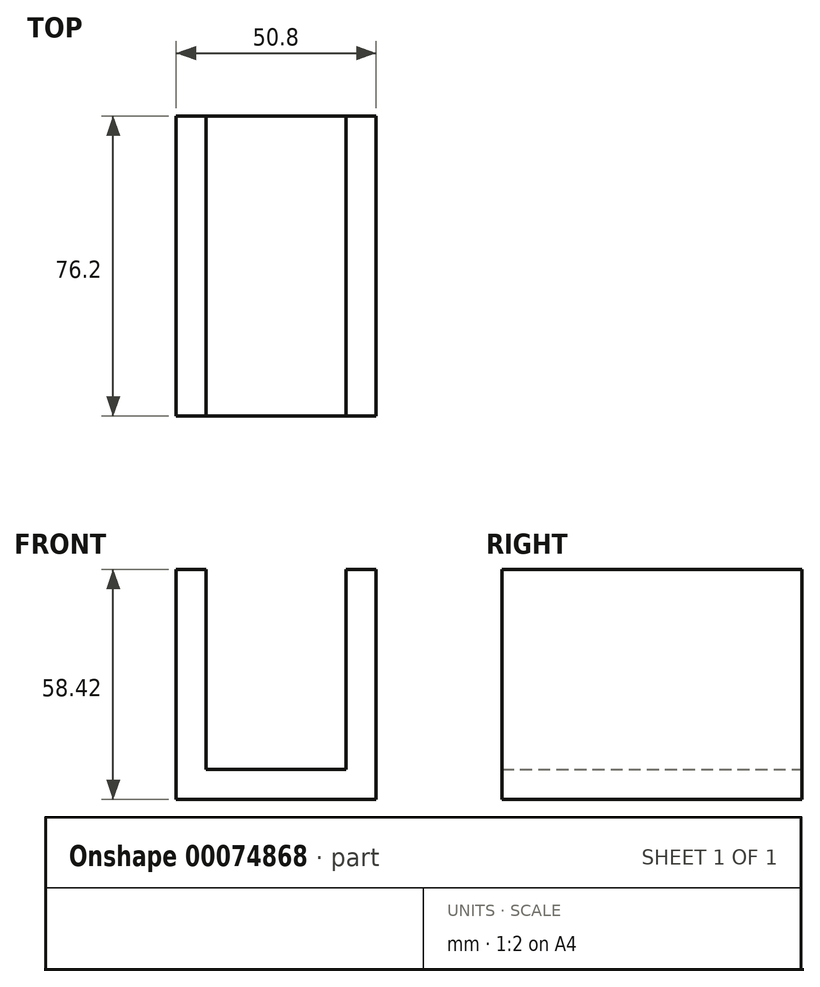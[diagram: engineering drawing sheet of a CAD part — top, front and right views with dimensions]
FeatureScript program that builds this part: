
annotation { "Feature Type Name" : "Feature", "Feature Type Description" : "" }
export const myFeature = defineFeature(function(context is Context, id is Id, definition is map)
    precondition{}
    {
        {
            var Q0;
            Q0=qCreatedBy(makeId("Front.planeOp"),FACE);
            var sketch = newSketch(context, id + "F0", { "sketchPlane" : qUnion([Q0])});
            skLineSegment(sketch, "E0.bottom", {"start": v(0, 0) * mm, "end": v(25.4, 0) * mm});
            skLineSegment(sketch, "E0.top", {"start": v(0, 7.62) * mm, "end": v(25.4, 7.62) * mm});
            skLineSegment(sketch, "E0.left", {"start": v(0, 0) * mm, "end": v(0, 7.62) * mm});
            skLineSegment(sketch, "E0.right", {"start": v(25.4, 0) * mm, "end": v(25.4, 7.62) * mm});
            skLineSegment(sketch, "E1.bottom", {"start": v(25.4, 7.62) * mm, "end": v(17.78, 7.62) * mm});
            skLineSegment(sketch, "E1.top", {"start": v(25.4, 58.42) * mm, "end": v(17.78, 58.42) * mm});
            skLineSegment(sketch, "E1.left", {"start": v(25.4, 7.62) * mm, "end": v(25.4, 58.42) * mm});
            skLineSegment(sketch, "E1.right", {"start": v(17.78, 7.62) * mm, "end": v(17.78, 58.42) * mm});
            skLineSegment(sketch, "E2.MirrorCS", {"start": v(-25.4, 58.42) * mm, "end": v(-17.78, 58.42) * mm});
            skLineSegment(sketch, "E3.MirrorCS", {"start": v(-17.78, 7.62) * mm, "end": v(-17.78, 58.42) * mm});
            skLineSegment(sketch, "E4.MirrorCS", {"start": v(-25.4, 7.62) * mm, "end": v(-25.4, 58.42) * mm});
            skLineSegment(sketch, "E5.MirrorCS", {"start": v(-25.4, 0) * mm, "end": v(-25.4, 7.62) * mm});
            skLineSegment(sketch, "E6.MirrorCS", {"start": v(0, 0) * mm, "end": v(-25.4, 0) * mm});
            skLineSegment(sketch, "E7.MirrorCS", {"start": v(0, 7.62) * mm, "end": v(-25.4, 7.62) * mm});
            skSolve(sketch);
        }
        {
            var Q0;
            Q0 = qSketchRegion(id + "F0", true);
            extrude(context, id + "F1", {"entities" : qUnion([Q0]), "depth" : 76.2 * mm});
        }
    });
